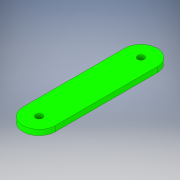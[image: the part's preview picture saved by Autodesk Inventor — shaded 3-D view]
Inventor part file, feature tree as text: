
AUTODESK INVENTOR PART (.ipt)
format: ipt  version: 2017 (Build 210142000, 142)  size: 114,688 bytes
history: native  units: in
note: dims shown in document units (in); Inventor stores cm internally (conversion verified against a paired STEP export)
features: extrude x1, sketch x1
ambient origin geometry x8: Origin, YZ Plane, XZ Plane, XY Plane, X Axis, Y Axis, Z Axis, Center Point
bodies: Solid1 (feature_tree)
feature tree (2):
  extrude  "Extrusion1"  Depth=0.75in
  sketch  "Sketch1"  dims[d0=1.5in d2=0.75in d6=0.0in]
